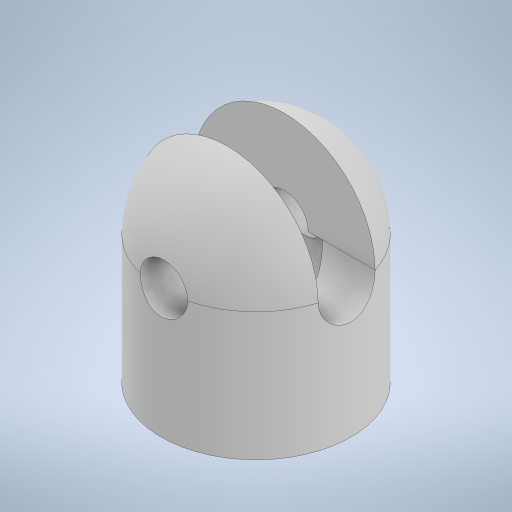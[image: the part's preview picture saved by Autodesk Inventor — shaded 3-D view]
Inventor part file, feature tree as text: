
AUTODESK INVENTOR PART (.ipt)
format: ipt  version: 2023.2 (Build 272271030, 271C)  size: 289,792 bytes
history: native  units: mm
features: projected_geometry x6, sketch x5, extrude x4, revolve x1
ambient origin geometry x8: Origin, YZ Plane, XZ Plane, XY Plane, X Axis, Y Axis, Z Axis, Center Point
bodies: Solid1 (feature_tree)
feature tree (16):
  extrude  "Extrusion1"  Depth=27.0mm TaperAngle=0.0deg
  revolve  "Revolution1"  Angle=180.0deg
  extrude  "Extrusion2"  TaperAngle=0.0deg  [1 undecoded]
  extrude  "Extrusion3"  Depth=20.268441mm
  extrude  "Extrusion4"  Depth=20.0mm
  sketch  "Sketch1"  dims[d0=40.0mm d1=27.0mm d2=0.0mm]
  sketch  "Sketch2"  dims[d3=40.0mm d4=180.0deg]
  projected_geometry  "Projected Loop1"
  sketch  "Sketch3"  dims[d5=10.0mm d6=0.0mm d7=0.0mm]
  projected_geometry  "Projected Loop2"
  projected_geometry  "Projected Loop3"
  sketch  "Sketch4"  dims[d8=12.0mm d9=20.268441mm]
  projected_geometry  "Projected Loop4"
  projected_geometry  "Projected Loop5"
  projected_geometry  "Projected Loop6"
  sketch  "Sketch5"  dims[d10=0.0mm d11=0.0mm d12=20.0mm d13=22.0mm d14=0.0mm]
note: 1 required parameter value undecoded (feature->parameter linkage not recoverable at this tier; creation-order binding heuristic only, values carry confidence <= 0.55)
